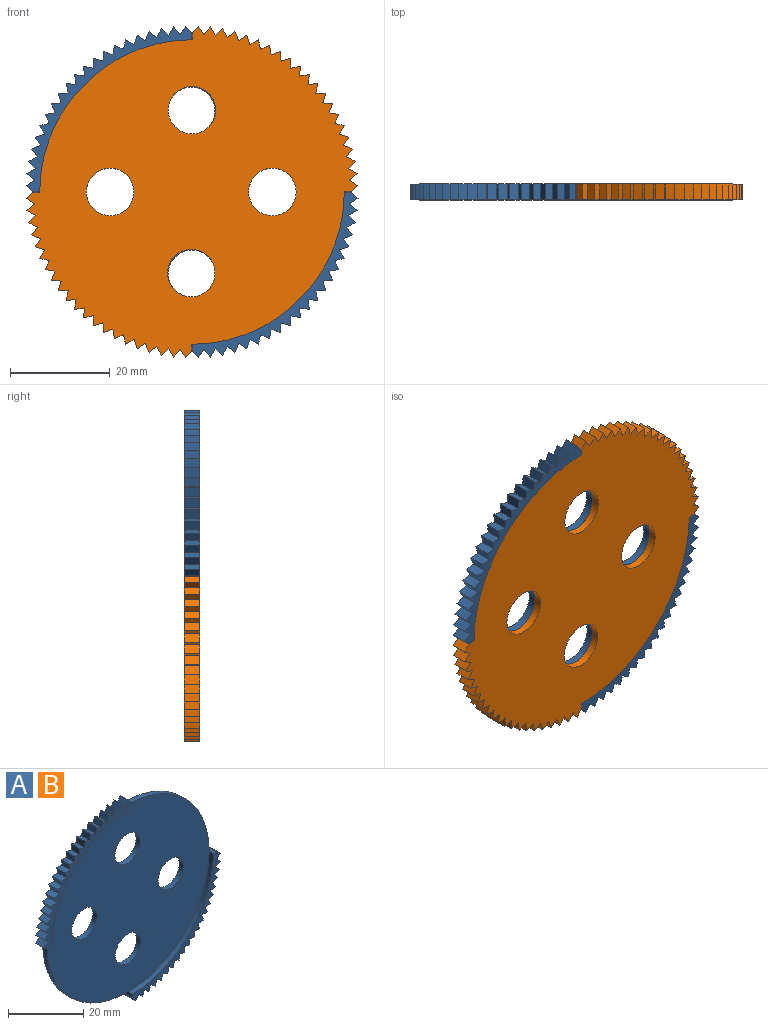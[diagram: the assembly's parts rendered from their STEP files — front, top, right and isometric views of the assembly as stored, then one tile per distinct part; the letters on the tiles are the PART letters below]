
ASSEMBLY  parts=2 mates=1
PART A: 100 faces, bbox 66.6x3.2x66.6 mm
  f0: plane 61.12x61.12mm, normal (0,-1,0), area 2648.8mm2, adj f2,f3,f4,f5,f7,f10,f98,f99
  f1: plane 66.63x66.63mm, normal (0,1,0), area 2844.2mm2, adj f2,f3,f4,f5,f6,f8,f11,f12
  f2: cylinder r=4.76mm len=9.53mm, axis (0,1,0), area 47.5mm2, adj f0,f1
  f3: cylinder r=4.76mm len=9.53mm, axis (0,1,0), area 47.5mm2, adj f0,f1
  f4: cylinder r=4.76mm len=9.53mm, axis (0,1,0), area 47.5mm2, adj f0,f1
  f5: cylinder r=4.76mm len=9.53mm, axis (0,1,0), area 47.5mm2, adj f0,f1
  f6: plane 3.18x1.19mm, normal (0,0,1), area 3.8mm2, adj f1,f7,f9,f97,f99
  f7: cylinder r=30.56mm len=30.56mm, axis (0,1,0), area 76.2mm2, adj f0,f6,f8,f9
  f8: plane 3.18x1.19mm, normal (-1,0,0), area 3.8mm2, adj f1,f7,f9,f61,f98
  f9: plane 33.31x33.31mm, normal (0,-1,0), area 97.7mm2, adj f6,f7,f8,f56,f57,f58,f59,f60
  f10: cylinder r=30.56mm len=30.56mm, axis (0,1,0), area 76.2mm2, adj f0,f11,f12,f13
  f11: plane 3.18x1.19mm, normal (1,0,0), area 3.8mm2, adj f1,f10,f13,f19,f99
  f12: plane 3.18x1.19mm, normal (0,0,-1), area 3.8mm2, adj f1,f10,f13,f54,f98
  f13: plane 33.31x33.31mm, normal (0,-1,0), area 97.7mm2, adj f10,f11,f12,f14,f15,f16,f17,f18
  f14: plane 3.18x1.73mm, normal (-0.87,0,0.5), area 6.4mm2, adj f1,f13,f15,f17
  f15: plane 3.18x1.47mm, normal (0.73,0,0.68), area 6.4mm2, adj f1,f13,f14,f18
  f16: plane 3.18x1.8mm, normal (-0.9,0,0.43), area 6.4mm2, adj f1,f13,f17,f21
  f17: plane 3.18x1.47mm, normal (0.68,0,0.73), area 6.4mm2, adj f1,f13,f14,f16
  f18: plane 3.18x1.65mm, normal (-0.83,0,0.56), area 6.4mm2, adj f1,f13,f15,f19
  f19: plane 3.18x1.56mm, normal (0.78,0,0.62), area 6.4mm2, adj f1,f11,f13,f18
  f20: plane 3.18x1.86mm, normal (-0.93,0,0.37), area 6.4mm2, adj f1,f13,f21,f23
  f21: plane 3.18x1.56mm, normal (0.62,0,0.78), area 6.4mm2, adj f1,f13,f16,f20
  f22: plane 3.18x1.91mm, normal (-0.96,0,0.29), area 6.4mm2, adj f1,f13,f23,f25
  f23: plane 3.18x1.65mm, normal (0.56,0,0.83), area 6.4mm2, adj f1,f13,f20,f22
  f24: plane 3.18x1.95mm, normal (-0.98,0,0.22), area 6.4mm2, adj f1,f13,f25,f27
  f25: plane 3.18x1.73mm, normal (0.5,0,0.87), area 6.4mm2, adj f1,f13,f22,f24
  f26: plane 3.18x1.98mm, normal (-0.99,0,0.15), area 6.4mm2, adj f1,f13,f27,f29
  f27: plane 3.18x1.8mm, normal (0.43,0,0.9), area 6.4mm2, adj f1,f13,f24,f26
  f28: plane 3.18x1.99mm, normal (-1,0,0.07), area 6.4mm2, adj f1,f13,f29,f31
  f29: plane 3.18x1.86mm, normal (0.37,0,0.93), area 6.4mm2, adj f1,f13,f26,f28
  f30: plane 3.18x2mm, normal (-1,0,0), area 6.4mm2, adj f1,f13,f31,f33
  f31: plane 3.18x1.91mm, normal (0.3,0,0.96), area 6.4mm2, adj f1,f13,f28,f30
  f32: plane 3.18x1.99mm, normal (-1,0,-0.08), area 6.4mm2, adj f1,f13,f33,f35
  f33: plane 3.18x1.95mm, normal (0.22,0,0.97), area 6.4mm2, adj f1,f13,f30,f32
  f34: plane 3.18x1.98mm, normal (-0.99,0,-0.15), area 6.4mm2, adj f1,f13,f35,f37
  f35: plane 3.18x1.98mm, normal (0.15,0,0.99), area 6.4mm2, adj f1,f13,f32,f34
  f36: plane 3.18x1.95mm, normal (-0.97,0,-0.22), area 6.4mm2, adj f1,f13,f37,f39
  f37: plane 3.18x1.99mm, normal (0.08,0,1), area 6.4mm2, adj f1,f13,f34,f36
  f38: plane 3.18x1.91mm, normal (-0.96,0,-0.3), area 6.4mm2, adj f1,f13,f39,f41
  f39: plane 3.18x2mm, normal (0,0,1), area 6.4mm2, adj f1,f13,f36,f38
  f40: plane 3.18x1.86mm, normal (-0.93,0,-0.37), area 6.4mm2, adj f1,f13,f41,f43
  f41: plane 3.18x1.99mm, normal (-0.07,0,1), area 6.4mm2, adj f1,f13,f38,f40
  f42: plane 3.18x1.8mm, normal (-0.9,0,-0.43), area 6.4mm2, adj f1,f13,f43,f45
  f43: plane 3.18x1.98mm, normal (-0.15,0,0.99), area 6.4mm2, adj f1,f13,f40,f42
  f44: plane 3.18x1.73mm, normal (-0.87,0,-0.5), area 6.4mm2, adj f1,f13,f45,f47
  f45: plane 3.18x1.95mm, normal (-0.22,0,0.98), area 6.4mm2, adj f1,f13,f42,f44
  f46: plane 3.18x1.65mm, normal (-0.83,0,-0.56), area 6.4mm2, adj f1,f13,f47,f49
  f47: plane 3.18x1.91mm, normal (-0.29,0,0.96), area 6.4mm2, adj f1,f13,f44,f46
  f48: plane 3.18x1.56mm, normal (-0.78,0,-0.62), area 6.4mm2, adj f1,f13,f49,f51
  f49: plane 3.18x1.86mm, normal (-0.37,0,0.93), area 6.4mm2, adj f1,f13,f46,f48
  f50: plane 3.18x1.47mm, normal (-0.73,0,-0.68), area 6.4mm2, adj f1,f13,f51,f53
  f51: plane 3.18x1.8mm, normal (-0.43,0,0.9), area 6.4mm2, adj f1,f13,f48,f50
  f52: plane 3.18x1.47mm, normal (-0.68,0,-0.73), area 6.4mm2, adj f1,f13,f53,f55
  f53: plane 3.18x1.73mm, normal (-0.5,0,0.87), area 6.4mm2, adj f1,f13,f50,f52
  f54: plane 3.18x1.56mm, normal (-0.62,0,-0.78), area 6.4mm2, adj f1,f12,f13,f55
  f55: plane 3.18x1.65mm, normal (-0.56,0,0.83), area 6.4mm2, adj f1,f13,f52,f54
  f56: plane 3.18x1.73mm, normal (0.87,0,-0.5), area 6.4mm2, adj f1,f9,f57,f59
  f57: plane 3.18x1.47mm, normal (-0.73,0,-0.68), area 6.4mm2, adj f1,f9,f56,f60
  f58: plane 3.18x1.8mm, normal (0.9,0,-0.43), area 6.4mm2, adj f1,f9,f59,f63
  f59: plane 3.18x1.47mm, normal (-0.68,0,-0.73), area 6.4mm2, adj f1,f9,f56,f58
  f60: plane 3.18x1.65mm, normal (0.83,0,-0.56), area 6.4mm2, adj f1,f9,f57,f61
  f61: plane 3.18x1.56mm, normal (-0.78,0,-0.62), area 6.4mm2, adj f1,f8,f9,f60
  f62: plane 3.18x1.86mm, normal (0.93,0,-0.37), area 6.4mm2, adj f1,f9,f63,f65
  f63: plane 3.18x1.56mm, normal (-0.62,0,-0.78), area 6.4mm2, adj f1,f9,f58,f62
  f64: plane 3.18x1.91mm, normal (0.96,0,-0.29), area 6.4mm2, adj f1,f9,f65,f67
  f65: plane 3.18x1.65mm, normal (-0.56,0,-0.83), area 6.4mm2, adj f1,f9,f62,f64
  f66: plane 3.18x1.95mm, normal (0.98,0,-0.22), area 6.4mm2, adj f1,f9,f67,f69
  f67: plane 3.18x1.73mm, normal (-0.5,0,-0.87), area 6.4mm2, adj f1,f9,f64,f66
  f68: plane 3.18x1.98mm, normal (0.99,0,-0.15), area 6.4mm2, adj f1,f9,f69,f71
  f69: plane 3.18x1.8mm, normal (-0.43,0,-0.9), area 6.4mm2, adj f1,f9,f66,f68
  f70: plane 3.18x1.99mm, normal (1,0,-0.07), area 6.4mm2, adj f1,f9,f71,f73
  f71: plane 3.18x1.86mm, normal (-0.37,0,-0.93), area 6.4mm2, adj f1,f9,f68,f70
  f72: plane 3.18x2mm, normal (1,0,0), area 6.4mm2, adj f1,f9,f73,f75
  f73: plane 3.18x1.91mm, normal (-0.3,0,-0.96), area 6.4mm2, adj f1,f9,f70,f72
  f74: plane 3.18x1.99mm, normal (1,0,0.08), area 6.4mm2, adj f1,f9,f75,f77
  f75: plane 3.18x1.95mm, normal (-0.22,0,-0.97), area 6.4mm2, adj f1,f9,f72,f74
  f76: plane 3.18x1.98mm, normal (0.99,0,0.15), area 6.4mm2, adj f1,f9,f77,f79
  f77: plane 3.18x1.98mm, normal (-0.15,0,-0.99), area 6.4mm2, adj f1,f9,f74,f76
  f78: plane 3.18x1.95mm, normal (0.97,0,0.22), area 6.4mm2, adj f1,f9,f79,f81
  f79: plane 3.18x1.99mm, normal (-0.08,0,-1), area 6.4mm2, adj f1,f9,f76,f78
  f80: plane 3.18x1.91mm, normal (0.96,0,0.3), area 6.4mm2, adj f1,f9,f81,f83
  f81: plane 3.18x2mm, normal (0,0,-1), area 6.4mm2, adj f1,f9,f78,f80
  f82: plane 3.18x1.86mm, normal (0.93,0,0.37), area 6.4mm2, adj f1,f9,f83,f85
  f83: plane 3.18x1.99mm, normal (0.07,0,-1), area 6.4mm2, adj f1,f9,f80,f82
  f84: plane 3.18x1.8mm, normal (0.9,0,0.43), area 6.4mm2, adj f1,f9,f85,f87
  f85: plane 3.18x1.98mm, normal (0.15,0,-0.99), area 6.4mm2, adj f1,f9,f82,f84
  f86: plane 3.18x1.73mm, normal (0.87,0,0.5), area 6.4mm2, adj f1,f9,f87,f89
  f87: plane 3.18x1.95mm, normal (0.22,0,-0.98), area 6.4mm2, adj f1,f9,f84,f86
  f88: plane 3.18x1.65mm, normal (0.83,0,0.56), area 6.4mm2, adj f1,f9,f89,f91
  f89: plane 3.18x1.91mm, normal (0.29,0,-0.96), area 6.4mm2, adj f1,f9,f86,f88
  f90: plane 3.18x1.56mm, normal (0.78,0,0.62), area 6.4mm2, adj f1,f9,f91,f93
  f91: plane 3.18x1.86mm, normal (0.37,0,-0.93), area 6.4mm2, adj f1,f9,f88,f90
  f92: plane 3.18x1.47mm, normal (0.73,0,0.68), area 6.4mm2, adj f1,f9,f93,f95
  f93: plane 3.18x1.8mm, normal (0.43,0,-0.9), area 6.4mm2, adj f1,f9,f90,f92
  f94: plane 3.18x1.47mm, normal (0.68,0,0.73), area 6.4mm2, adj f1,f9,f95,f96
  f95: plane 3.18x1.73mm, normal (0.5,0,-0.87), area 6.4mm2, adj f1,f9,f92,f94
  f96: plane 3.18x1.65mm, normal (0.56,0,-0.83), area 6.4mm2, adj f1,f9,f94,f97
  f97: plane 3.18x1.56mm, normal (0.62,0,0.78), area 6.4mm2, adj f1,f6,f9,f96
  f98: cylinder r=30.56mm len=30.56mm, axis (0,-1,0), area 76.2mm2, adj f0,f1,f8,f12
  f99: cylinder r=30.56mm len=30.56mm, axis (0,-1,0), area 76.2mm2, adj f0,f1,f6,f11
PART B: same geometry as A
PLACE A t=(-0.38,6.09,7.08)mm
PLACE B rot(axis=(1,0,0),180deg) t=(-0.38,2.92,7.08)mm
MATE fastened B.f10 <-> A.f98  axis (0,1,0) through (-0.38,6.09,7.08)mm
